# Revit family: BC_Hitachi_RAS-4-6FS(V)NME_LOD400
name_source: partatom
category: Equipement de génie climatique
revit_build: Autodesk Revit 2017 (Build: 20160225_1515(x64)
units: mm (PartAtom-declared; Revit-internal decimal feet)

## family parameters
Basée sur le plan de construction = Non
Cote de connecteur circulaire = Utiliser le diamètre
Couper avec des vides une fois chargée = Non
Numéro OmniClass = 23.75.00.00
Partagée = Non
Point de calcul de pièce = Non
Titre OmniClass = Climate Control (HVAC)
Toujours verticalement = Oui
Type d'élément = Normal

## types (6) — shared parameters
Approximate Packing Volume = 0.71 m³
BC_MODEL_ID = 167019
BC_OBJECT_ID = 29707
BC_OBJECT_VERSION = #3
Color = Natural Grey (1.0Y8.5/0.5)
Compressor Quantity = 1
Compressor Type = SHEC Rotary
Condenser Fan Quantity = 2
Condenser Fan Type = Axial
Fabricant = Hitachi Air Conditioning Europe SAS
Flow Control = Micro-Computer control expansion valve
Frequency = 50 Hz
Gas Diameter = 15.88 mm
Heat Exchanger = Multi Pass Cross - Finned Tube
Liquid Diameter = 9.52 mm
Modèle = Set Free Mini - RAS-4-6 FS(V)NME
Motor - Number of Poles = 4
Nominal Air Flow = 8700.0 m³/h
Nominal Static Pressure = 30.0 Pa
Overall Depth = 370.00 mm
Overall Height = 1380.00 mm
Overall Width = 950.00 mm
Packing dimensions (H x W x D) = 1515 mm x 1012 mm x 460 mm
Refrigerant Type = R410
Refrigeration Oil Charge = 1.65 L/Unit
Refrigeration Oil Type = α 68HES-H

## per-type parameters (varying)
| type | BC_VARIANT_ID | Compressor Model | Cooling Capacity | Gross Weight | Heating Capacity | Motor power | Net Weight | Nominal Voltage | Number of Poles | Refrigerant charge before shipment | Sound Pressure Level (night mode) | Sound level |
| RAS-4FSVNME | 193005 | ATH356 | 12 kW | 124.00 kg | 13 kW | 3 kW | 114.00 kg | 230 V | 1 | 3.70 kg | 52 (45) | 69 |
| RAS-5FSVNME | 193006 | ATH420 | 14 kW | 128.00 kg | 16 kW | 4 kW | 118.00 kg | 230 V | 1 | 4.10 kg | 52 (47) | 69 |
| RAS-6FSVNME | 193008 | ATH420 | 16 kW | 128.00 kg | 18 kW | 4 kW | 118.00 kg | 230 V | 1 | 4.10 kg | 53 (48) | 70 |
| RAS-4FSNME | 193053 | ATH356 | 12 kW | 125.00 kg | 13 kW | 3 kW | 115.00 kg | 400 V | 3 | 3.70 kg | 52 (45) | 69 |
| RAS-5FSNME | 193052 | ATH420 | 14 kW | 129.00 kg | 16 kW | 4 kW | 119.00 kg | 400 V | 3 | 4.10 kg | 52 (47) | 69 |
| RAS-6FSNME | 193051 | ATH420 | 16 kW | 129.00 kg | 18 kW | 4 kW | 119.00 kg | 400 V | 3 | 4.10 kg | 53 (48) | 70 |

note: column(s) folded — value = type name in every type: Commentaires du type, Designation, Reference

## geometry (parser evidence)
native form markers: Blend x2
no freeform markers — native parametric forms only
